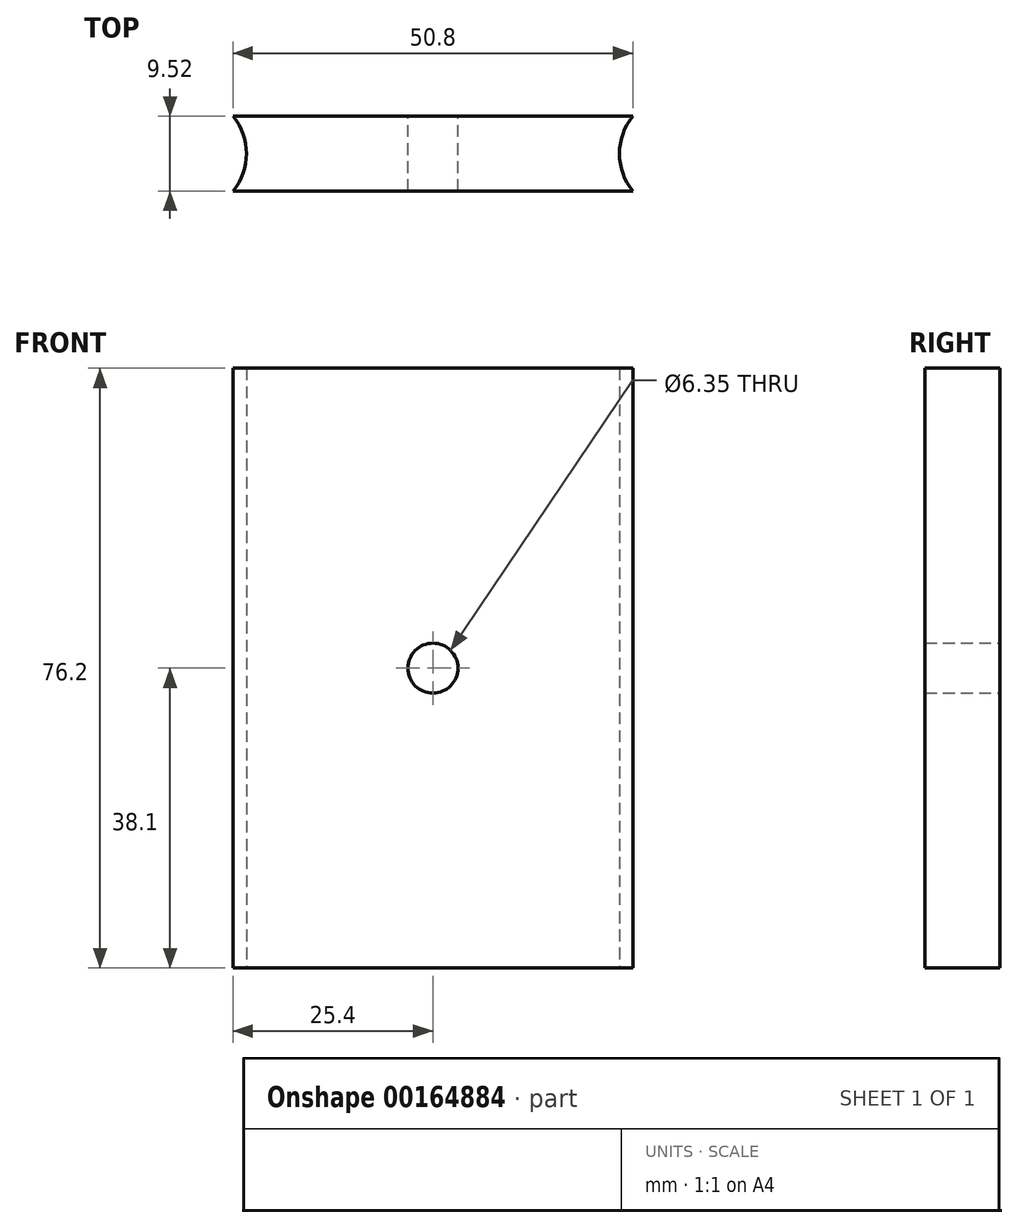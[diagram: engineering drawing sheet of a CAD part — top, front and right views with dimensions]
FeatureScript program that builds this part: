
annotation { "Feature Type Name" : "Feature", "Feature Type Description" : "" }
export const myFeature = defineFeature(function(context is Context, id is Id, definition is map)
    precondition{}
    {
        {
            var Q0;
            Q0=qCreatedBy(makeId("Top.planeOp"),FACE);
            var sketch = newSketch(context, id + "F0", { "sketchPlane" : qUnion([Q0])});
            skLineSegment(sketch, "E0.bottom", {"start": v(25.4, -4.76) * mm, "end": v(-25.4, -4.76) * mm});
            skLineSegment(sketch, "E0.top", {"start": v(25.4, 4.76) * mm, "end": v(-25.4, 4.76) * mm});
            skLineSegment(sketch, "E0.left", {"start": v(25.4, -4.76) * mm, "end": v(25.4, 4.76) * mm, "construction": true});
            skLineSegment(sketch, "E0.right", {"start": v(-25.4, -4.76) * mm, "end": v(-25.4, 4.76) * mm, "construction": true});
            skPoint(sketch, "E0.middle", {"position": v(0, 0) * mm});
            skArc(sketch, "E1", {"start": v(-25.4, -4.76) * mm, "mid": v(-23.7, 0) * mm, "end": v(-25.4, 4.76) * mm});
            skArc(sketch, "E2", {"start": v(25.4, 4.76) * mm, "mid": v(23.7, 0) * mm, "end": v(25.4, -4.76) * mm});
            skLineSegment(sketch, "E3", {"start": v(-31.2, 0) * mm, "end": v(31.2, 0) * mm, "construction": true});
            skSolve(sketch);
        }
        {
            var Q0;
            Q0 = qSketchRegion(id + "F0", true);
            extrude(context, id + "F1", {"entities" : qUnion([Q0]), "depth" : 76.2 * mm});
        }
        {
            var Q0;
            Q0=makeQuery(id+"F1.opExtrude","SWEPT_FACE",FACE,{"disambiguationData":[OSD([sQuery(id+"F0.wireOp",EDGE,"E0.top")])]});
            var sketch = newSketch(context, id + "F2", { "sketchPlane" : qUnion([Q0])});
            skLineSegment(sketch, "E4", {"start": v(25.4, 38.1) * mm, "end": v(-25.4, 38.1) * mm, "construction": true});
            skCircle(sketch, "E5", {"center": v(0, 38.1) * mm, "radius": 3.18 * mm});
            skSolve(sketch);
        }
        {
            var Q0;
            Q0 = qSketchRegion(id + "F2", true);
            var Q1;
            Q1=makeQuery(id+"F1.opExtrude","SWEPT_FACE",FACE,{"disambiguationData":[OSD([sQuery(id+"F0.wireOp",EDGE,"E0.bottom")])]});
            extrude(context, id + "F3", {"entities" : qUnion([Q0]), "operationType" : NewBodyOperationType.REMOVE, "endBound" : BoundingType.UP_TO_SURFACE, "oppositeDirection" : true, "endBoundEntityFace" : qUnion([Q1]), "depth" : 25.4 * mm});
        }
    });
